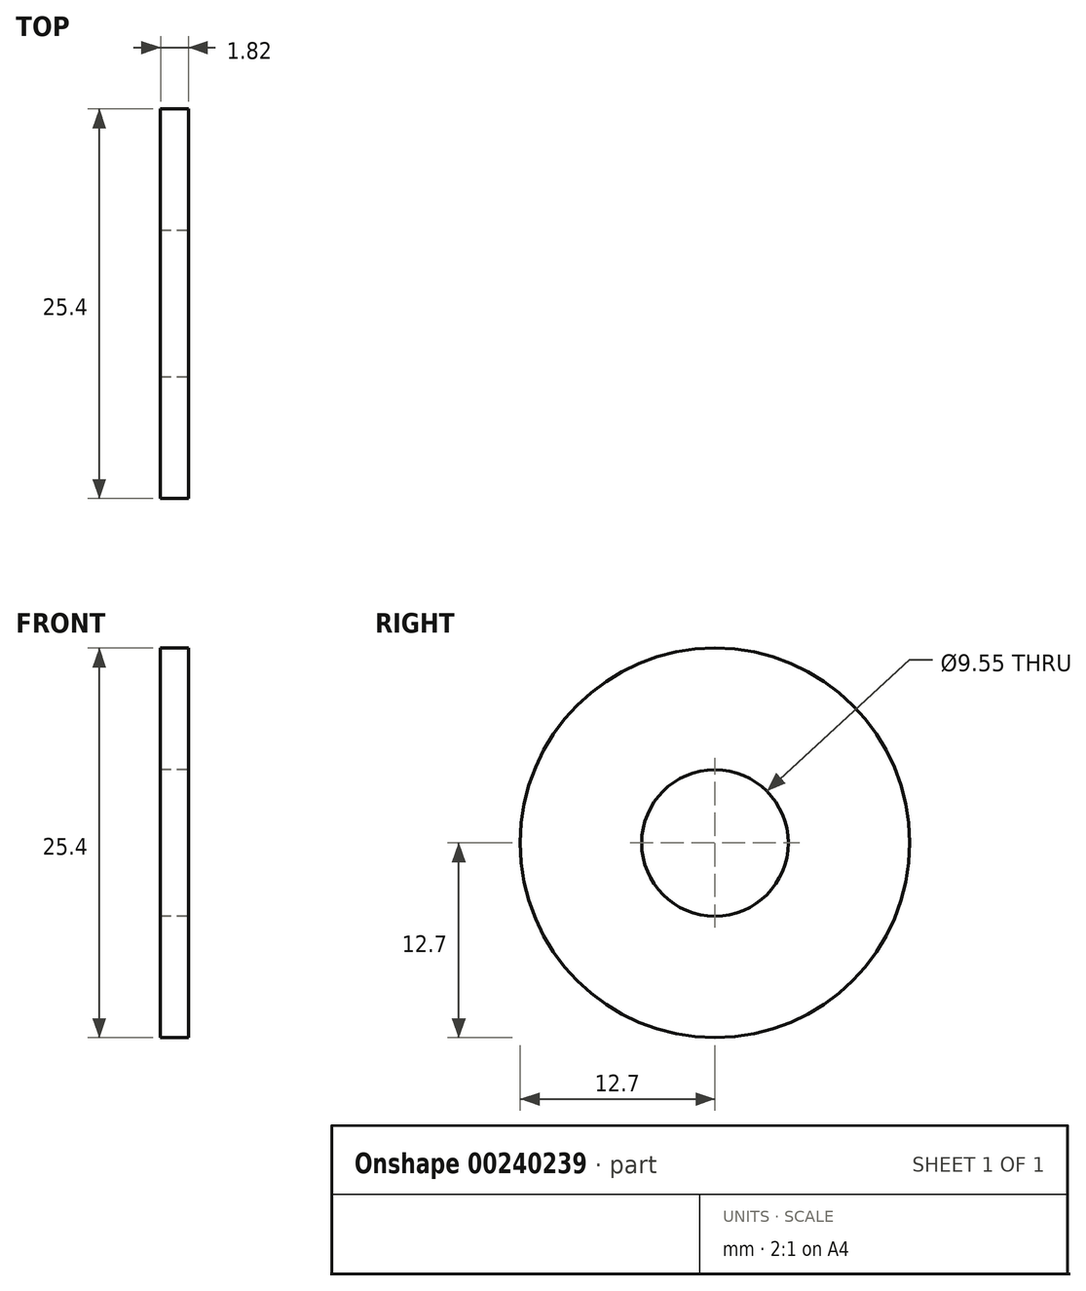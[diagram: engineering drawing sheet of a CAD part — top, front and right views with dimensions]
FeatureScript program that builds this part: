
annotation { "Feature Type Name" : "Feature", "Feature Type Description" : "" }
export const myFeature = defineFeature(function(context is Context, id is Id, definition is map)
    precondition{}
    {
        {
            var Q0;
            Q0=qCreatedBy(makeId("Right.planeOp"),FACE);
            var sketch = newSketch(context, id + "F0", { "sketchPlane" : qUnion([Q0])});
            skCircle(sketch, "E0", {"center": v(0, 0) * mm, "radius": 4.78 * mm});
            skCircle(sketch, "E1", {"center": v(0, 0) * mm, "radius": 12.7 * mm});
            skSolve(sketch);
        }
        {
            var Q0;
            Q0 = qSketchRegion(id + "F0", true);
            extrude(context, id + "F1", {"entities" : qUnion([Q0]), "endBound" : BoundingType.SYMMETRIC, "depth" : 1.83 * mm});
        }
    });
